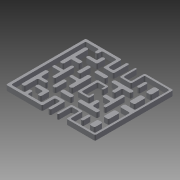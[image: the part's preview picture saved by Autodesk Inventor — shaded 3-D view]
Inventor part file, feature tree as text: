
AUTODESK INVENTOR PART (.ipt)
format: ipt  version: 2015 (Build 190159000, 159)  size: 593,920 bytes
history: native  units: in
note: dims shown in document units (in); Inventor stores cm internally (conversion verified against a paired STEP export)
features: fillet x4, extrude x1, sketch x1, other x1
ambient origin geometry x8: Origin, YZ Plane, XZ Plane, XY Plane, X Axis, Y Axis, Z Axis, Center Point
bodies: Solid1 (feature_tree)
feature tree (7):
  extrude  "Extrusion1"  Depth=0.0625in
  fillet  "Fillet1"  Radius=0.0625in
  fillet  "Fillet2"  Radius=0.0625in
  fillet  "Fillet3"  Radius=0.0625in
  fillet  "Fillet4"  [1 undecoded]
  sketch  "Sketch1"  dims[d11=0.25in d12=0.0in d13=0.0625in d14=0.0625in d15=0.0625in d16=0.0625in]
  other  "Image1"
note: 1 required parameter value undecoded (feature->parameter linkage not recoverable at this tier; creation-order binding heuristic only, values carry confidence <= 0.55)
